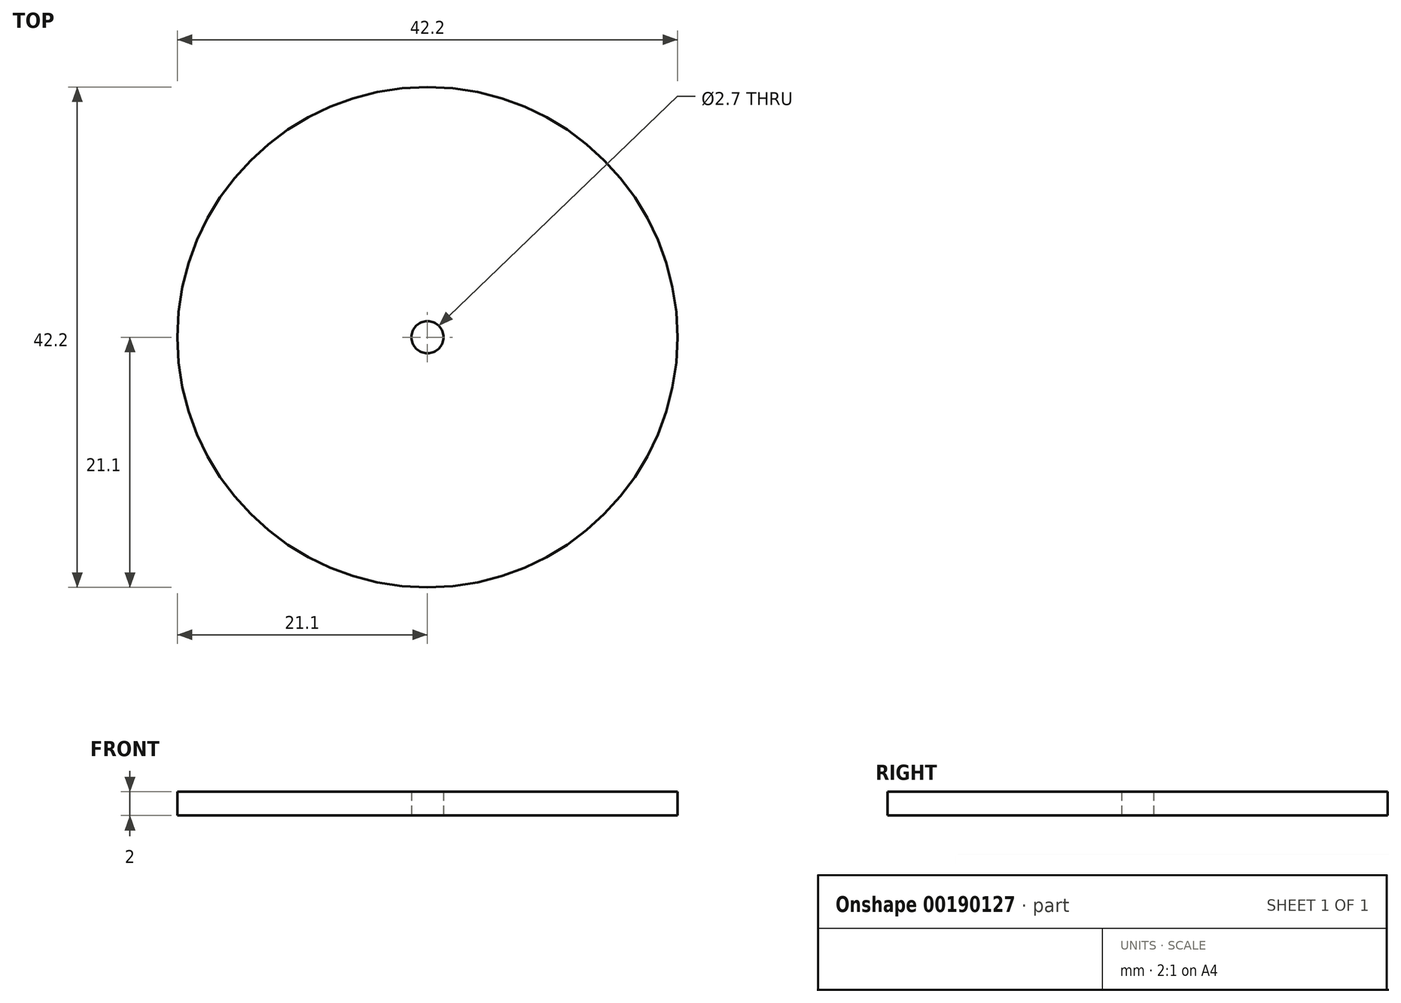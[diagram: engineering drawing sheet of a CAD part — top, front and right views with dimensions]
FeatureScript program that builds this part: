
annotation { "Feature Type Name" : "Feature", "Feature Type Description" : "" }
export const myFeature = defineFeature(function(context is Context, id is Id, definition is map)
    precondition{}
    {
        {
            var Q0;
            Q0=qCreatedBy(makeId("Top.planeOp"),FACE);
            var sketch = newSketch(context, id + "F0", { "sketchPlane" : qUnion([Q0])});
            skCircle(sketch, "E0", {"center": v(0, 0) * mm, "radius": 21.1 * mm});
            skCircle(sketch, "E1", {"center": v(0, 0) * mm, "radius": 1.35 * mm});
            skSolve(sketch);
        }
        {
            var Q0;
            Q0 = qSketchRegion(id + "F0", true);
            extrude(context, id + "F1", {"entities" : qUnion([Q0]), "depth" : 2 * mm});
        }
    });
